# Revit family: TPOne_V2_RFA
name_source: partatom
category: Data Devices
units: mm (PartAtom-declared; Revit-internal decimal feet)

## family parameters
Cut with Voids When Loaded = No
Host = Face
Maintain Annotation Orientation = Yes
Part Type = Normal
Room Calculation Point = No
Round Connector Dimension = Use Diameter
Shared = No

## types (6) — shared parameters
Ball Pressure Test = 75
Body Material = Danfoss Plastic White
Control Polution Situation = Degree 2
D = 30 mm  [stored 0.0984252 ft]
D-All = 9 mm  [stored 0.0295276 ft]
D1a = 6 mm  [stored 0.019685 ft]
D1b = 3 mm  [stored 0.00984252 ft]
D2 = 11 mm  [stored 0.0360892 ft]
Da = 1 mm  [stored 0.00328084 ft]
Default Elevation = 1219 mm
Description = Room Thermostat
H1_2 = 30 mm  [stored 0.0984252 ft]
H2_2 = 24 mm
H_2 = 33 mm
IfcExportAs = IfcElectricApplianceType
IfcExportType = TPOne
LOD 200 = No
LOD 350 = Yes
Manufacturer = Danfoss
Max Ambient Temperature = 45 °C
Max Temperature Setting = 35 °C
Min Temperature Setting = 5 °C
URL = https://store.danfoss.com
W1_2 = 74 mm  [stored 0.242782 ft]
W2_2 = 68 mm
W_2 = 78 mm  [stored 0.255906 ft]

## per-type parameters (varying)
| type | A | DBR | IP Rating | Maximum Range | Model | Model Type | Operating Frequency | Operating Temperature Range | Output Channel 1 | Output Channel 2 | Power Supply RT | RX1-S | Rated Impulse Voltage | Switch Rating Channel 1 | Transmission Frequency | Voltage | Weight |
| TPOne-B_087N7851 | 0 mm  [stored 0 ft] | No | IP20 | - | 087N7851 | TPOne-B | - | 0-45 °C | Volt free, SPDT type 1B | - | 2.5 - 3 VDC (2x AA Alkaline Batteries) | No | - | 3 A (1 A) at 230 VAC | - | 3 V | 0.27 kg |
| TPOne-M_087N7852 | 0 mm  [stored 0 ft] | No | IP20 | - | 087N7852 | TPOne-M | 50/60Hz | 0-45 °C | Volt free, SPDT type 1B | 3 A at 230 VAC | 230 VAC | No | 4 kV | 3 A (1 A) at 230 VAC | - | 230 V | 0.22 kg |
| TPOne-RF + RX1-S_V2_087N7858 | 1 mm  [stored 0.00328084 ft] | No | IP20 | 30 m | 087N7858 | TPOne-RF + RX1-S_V2 | - | 0-45 °C | Volt free, SPDT type 1B (RX1-S V2) | - | 2.5 - 3 VDC (2x AA Alkaline Batteries) | Yes | - | 3 A (1 A) at 230 VAC (RX1-S V2) | 433.92 Mhz | 230 V | 0.48 kg |
| TPOne-S+ DBR_087N7856 | 2 mm  [stored 0.00656168 ft] | Yes | IP20 | 30 m | 087N7856 | TPOne-S+ DBR | 50/60Hz | 0-45 °C | Volt free, SPST type 1A (DBR) | - | 230 VAC | No | 2.5 kV | 3 A (1 A) at 230 VAC (DBR) | 868.42 MHz | 230 V | 0.10 kg |
| TPOne-RF_087N7853 | 0 mm  [stored 0 ft] | No | IP20 | 30 m | 087N7853 | TPOne-RF | - | 0-45 °C | - | - | 2.5 -3 VDC (2x AA Alkaline Batteries) | No | - | - | 433.92 Mhz | 3 V | 0.27 kg |
| TPOne-OT_087N7859 | 0 mm  [stored 0 ft] | No | IP30 | - | 087N7859 | TPOne-OT | 50/60Hz | 0-40 °C | Data 24 V DC BUS | - | 24 VDC power line from boiler & 3 VDC (2x AA Alkaline Batteries) | No | 4 kV | - | - | 24 V | 0.22 kg |

note: source unit labels omitted for Ball Pressure Test — the stored unit's dimension contradicts the parameter name (converter mislabeling)

note: [stored X ft] marks values corroborated as IEEE doubles in the binary element streams (Revit-internal decimal feet)

## geometry (parser evidence)
native form markers: Sweep x6
no freeform markers — native parametric forms only
